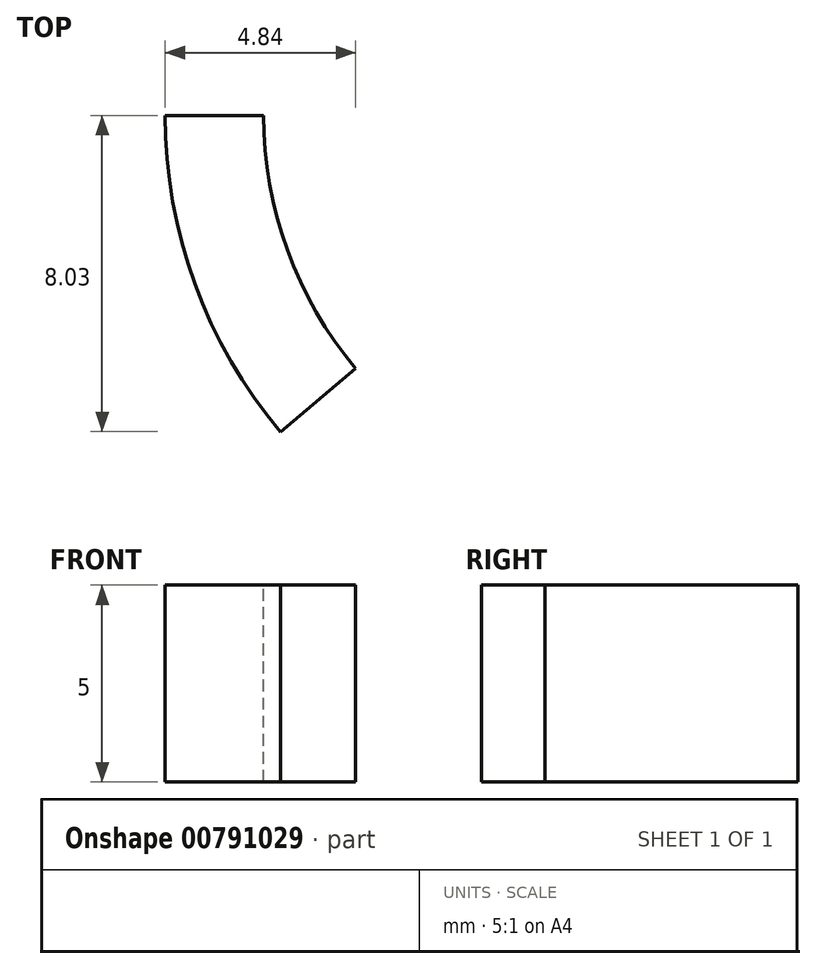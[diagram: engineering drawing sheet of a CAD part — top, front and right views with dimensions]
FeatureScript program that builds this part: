
annotation { "Feature Type Name" : "Feature", "Feature Type Description" : "" }
export const myFeature = defineFeature(function(context is Context, id is Id, definition is map)
    precondition{}
    {
        {
            var Q0;
            Q0=qCreatedBy(makeId("Front.planeOp"),FACE);
            var sketch = newSketch(context, id + "F0", { "sketchPlane" : qUnion([Q0])});
            skLineSegment(sketch, "E0.bottom", {"start": v(0, 0) * mm, "end": v(-2.5, 0) * mm});
            skLineSegment(sketch, "E0.top", {"start": v(0, 5) * mm, "end": v(-2.5, 5) * mm});
            skLineSegment(sketch, "E0.left", {"start": v(0, 0) * mm, "end": v(0, 5) * mm});
            skLineSegment(sketch, "E0.right", {"start": v(-2.5, 0) * mm, "end": v(-2.5, 5) * mm});
            skLineSegment(sketch, "E1", {"start": v(0, 0) * mm, "end": v(10, 0) * mm});
            skLineSegment(sketch, "E2", {"start": v(10, 0) * mm, "end": v(10, 21.04) * mm});
            skSolve(sketch);
        }
        {
            var Q0;
            Q0 = qSketchRegion(id + "F0", true);
            var Q1;
            Q1=sQuery(id+"F0.wireOp",EDGE,"E2");
            revolve(context, id + "F1", {"surfaceOperationType" : NewSurfaceOperationType.NEW, "entities" : qUnion([Q0]), "axis" : qUnion([Q1]), "revolveType" : RevolveType.ONE_DIRECTION, "angle" : 40 * degree});
        }
    });
